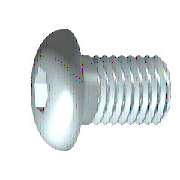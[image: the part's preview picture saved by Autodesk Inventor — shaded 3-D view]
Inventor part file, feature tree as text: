
AUTODESK INVENTOR PART (.ipt)
format: ipt  version: 2015 (Build 190159000, 159)  size: 200,192 bytes
history: native  units: mm (DEFAULTED — no unit token found)
features: sketch x2, extrude x1, plane x1, fillet x1
ambient origin geometry x7: Origin, YZ Plane, XY Plane, X Axis, Y Axis, Z Axis, Center Point
bodies: Solid1 (feature_tree), Body (feature_tree)
feature tree (5):
  extrude  "Slot"  Depth=3.3528mm
  plane  "Work Plane1"
  fillet  "Fillet2"  Radius=3.3528mm
  sketch  "Sketch1"  dims[d1=13.3348mm d2=2.5401mm d3=3.3528mm]
  sketch  "Sketch2"  dims[d4=2.2098mm d5=60.0deg d6=6.35mm d7=6.35mm d8=4.575385mm d9=11.0998mm d10=90.0deg d11=10.0mm d12=0.0mm d13=13.3348mm d14=0.0mm d15=0.779018mm d16=0.779018mm d17=2.9718mm d19=0.0mm d26=15.875mm d27=45.0deg d28=0.0mm d29=0.0mm d30=0.1mm]
